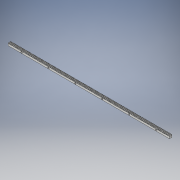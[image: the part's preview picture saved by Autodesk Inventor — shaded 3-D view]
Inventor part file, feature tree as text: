
AUTODESK INVENTOR PART (.ipt)
format: ipt  version: 2018 (Build 220112000, 112)  size: 1,214,464 bytes
history: native  units: in
note: dims shown in document units (in); Inventor stores cm internally (conversion verified against a paired STEP export)
features: extrude x1, sketch x1, other x1
ambient origin geometry x8: Origin, YZ Plane, XZ Plane, XY Plane, X Axis, Y Axis, Z Axis, Center Point
bodies: Solid1 (feature_tree)
feature tree (3):
  extrude  "Extrusion1"  Depth=2.0in
  sketch  "Sketch1"  dims[d0=24.0in d1=2.0in d2=1.0in d3=0.0in]
  other  "LPattern2"
